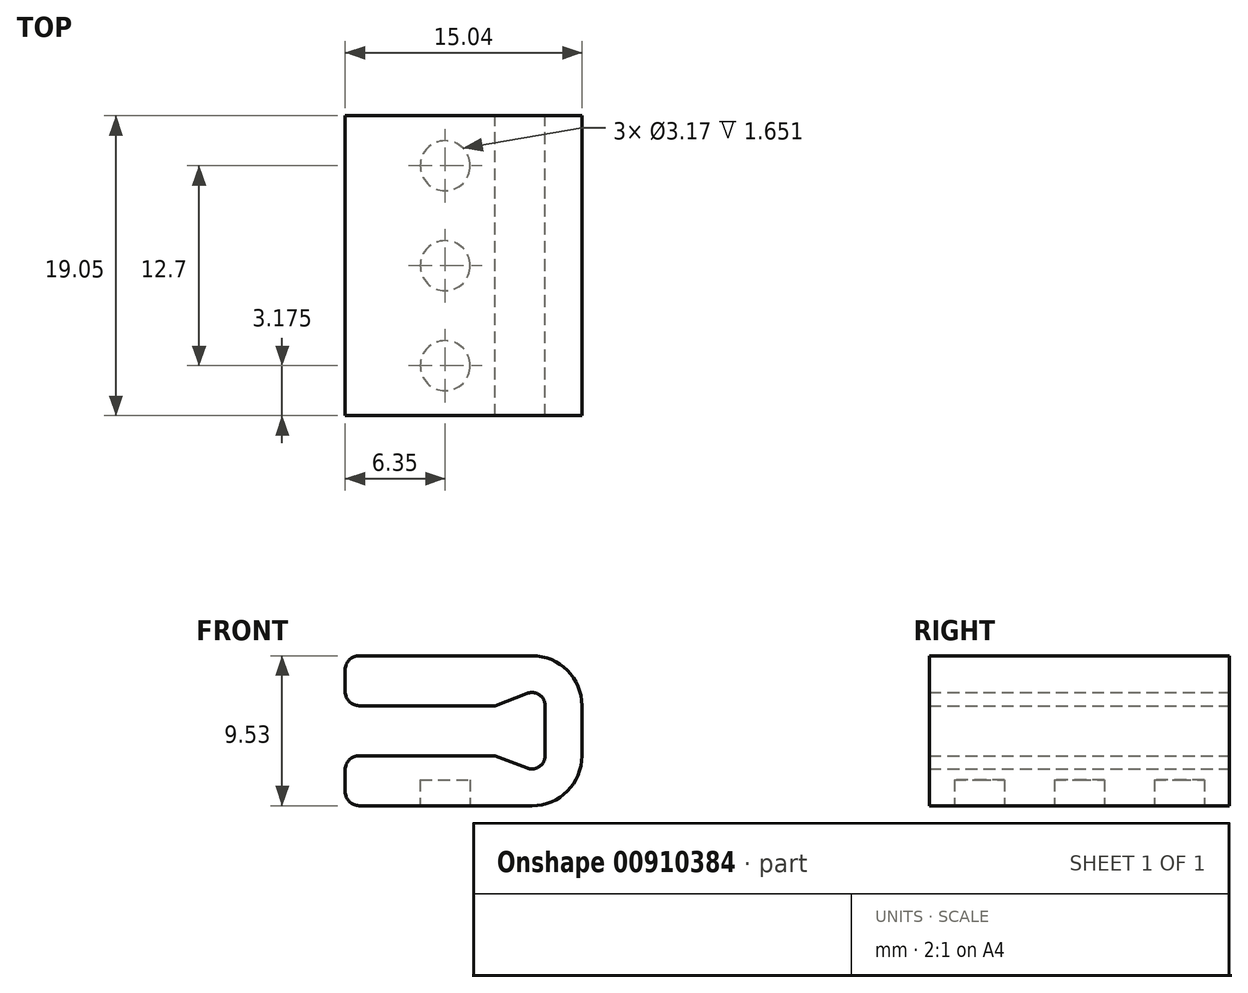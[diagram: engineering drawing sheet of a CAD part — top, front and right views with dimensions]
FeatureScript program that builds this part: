
annotation { "Feature Type Name" : "Feature", "Feature Type Description" : "" }
export const myFeature = defineFeature(function(context is Context, id is Id, definition is map)
    precondition{}
    {
        {
            var Q0;
            Q0=qCreatedBy(makeId("Front.planeOp"),FACE);
            var sketch = newSketch(context, id + "F0", { "sketchPlane" : qUnion([Q0])});
            skLineSegment(sketch, "E0", {"start": v(0, 0) * mm, "end": v(0, 3.18) * mm});
            skLineSegment(sketch, "E1", {"start": v(-11.81, 3.18) * mm, "end": v(-3.18, 3.18) * mm});
            skLineSegment(sketch, "E2", {"start": v(-12.7, 4.06) * mm, "end": v(-12.7, 5.46) * mm});
            skLineSegment(sketch, "E3", {"start": v(-11.81, 6.35) * mm, "end": v(-0.84, 6.35) * mm});
            skLineSegment(sketch, "E4", {"start": v(-0.84, -3.17) * mm, "end": v(-11.81, -3.17) * mm});
            skLineSegment(sketch, "E5", {"start": v(-12.7, -2.29) * mm, "end": v(-12.7, -0.89) * mm});
            skLineSegment(sketch, "E6", {"start": v(-11.81, 0) * mm, "end": v(-3.18, 0) * mm});
            skArc(sketch, "E7", {"start": v(0, 3.18) * mm, "mid": v(-0.36, 3.87) * mm, "end": v(-1.14, 3.96) * mm});
            skArc(sketch, "E8", {"start": v(0, 0) * mm, "mid": v(-0.36, -0.7) * mm, "end": v(-1.14, -0.78) * mm});
            skLineSegment(sketch, "E9", {"start": v(-1.14, 3.96) * mm, "end": v(-3.18, 3.18) * mm});
            skLineSegment(sketch, "E10", {"start": v(-1.14, -0.78) * mm, "end": v(-3.18, 0) * mm});
            skArc(sketch, "E11", {"start": v(-0.84, 6.35) * mm, "mid": v(1.4, 5.42) * mm, "end": v(2.34, 3.18) * mm});
            skArc(sketch, "E12", {"start": v(-0.84, -3.17) * mm, "mid": v(1.4, -2.25) * mm, "end": v(2.34, 0) * mm});
            skLineSegment(sketch, "E13", {"start": v(2.34, 3.18) * mm, "end": v(2.34, 0) * mm});
            skPoint(sketch, "E14.visualSharp", {"position": v(-12.7, 6.35) * mm});
            skArc(sketch, "E14.filletArc", {"start": v(-11.81, 6.35) * mm, "mid": v(-12.44, 6.09) * mm, "end": v(-12.7, 5.46) * mm});
            skPoint(sketch, "E15.visualSharp", {"position": v(-12.7, -3.18) * mm});
            skArc(sketch, "E15.filletArc", {"start": v(-12.7, -2.29) * mm, "mid": v(-12.44, -2.91) * mm, "end": v(-11.81, -3.18) * mm});
            skPoint(sketch, "E16.visualSharp", {"position": v(-12.7, 3.18) * mm});
            skArc(sketch, "E16.filletArc", {"start": v(-12.7, 4.06) * mm, "mid": v(-12.44, 3.44) * mm, "end": v(-11.81, 3.18) * mm});
            skPoint(sketch, "E17.visualSharp", {"position": v(-12.7, 0) * mm});
            skArc(sketch, "E17.filletArc", {"start": v(-11.81, 0) * mm, "mid": v(-12.44, -0.26) * mm, "end": v(-12.7, -0.89) * mm});
            skSolve(sketch);
        }
        {
            var Q0;
            Q0 = qSketchRegion(id + "F0", true);
            extrude(context, id + "F1", {"entities" : qUnion([Q0]), "depth" : 19.05 * mm, "offsetDistance" : 25.4 * mm});
        }
        {
            var Q0;
            Q0=makeQuery(id+"F1.opExtrude","SWEPT_FACE",FACE,{"disambiguationData":[OSD([sQuery(id+"F0.wireOp",EDGE,"E4")])]});
            var sketch = newSketch(context, id + "F2", { "sketchPlane" : qUnion([Q0])});
            skCircle(sketch, "E18", {"center": v(-6.35, 15.88) * mm, "radius": 1.59 * mm});
            skCircle(sketch, "E19", {"center": v(-6.35, 3.18) * mm, "radius": 1.59 * mm});
            skCircle(sketch, "E20", {"center": v(-6.35, 9.53) * mm, "radius": 1.59 * mm});
            skLineSegment(sketch, "E21", {"start": v(-11.81, 9.53) * mm, "end": v(-6.35, 9.53) * mm, "construction": true});
            skLineSegment(sketch, "E22", {"start": v(-6.35, 15.88) * mm, "end": v(-6.35, 9.53) * mm, "construction": true});
            skLineSegment(sketch, "E23", {"start": v(-6.35, 3.18) * mm, "end": v(-6.35, 9.53) * mm, "construction": true});
            skSolve(sketch);
        }
        {
            var Q0;
            Q0 = qSketchRegion(id + "F2", true);
            extrude(context, id + "F3", {"entities" : qUnion([Q0]), "operationType" : NewBodyOperationType.REMOVE, "oppositeDirection" : true, "depth" : 1.65 * mm, "offsetDistance" : 25.4 * mm});
        }
    });
